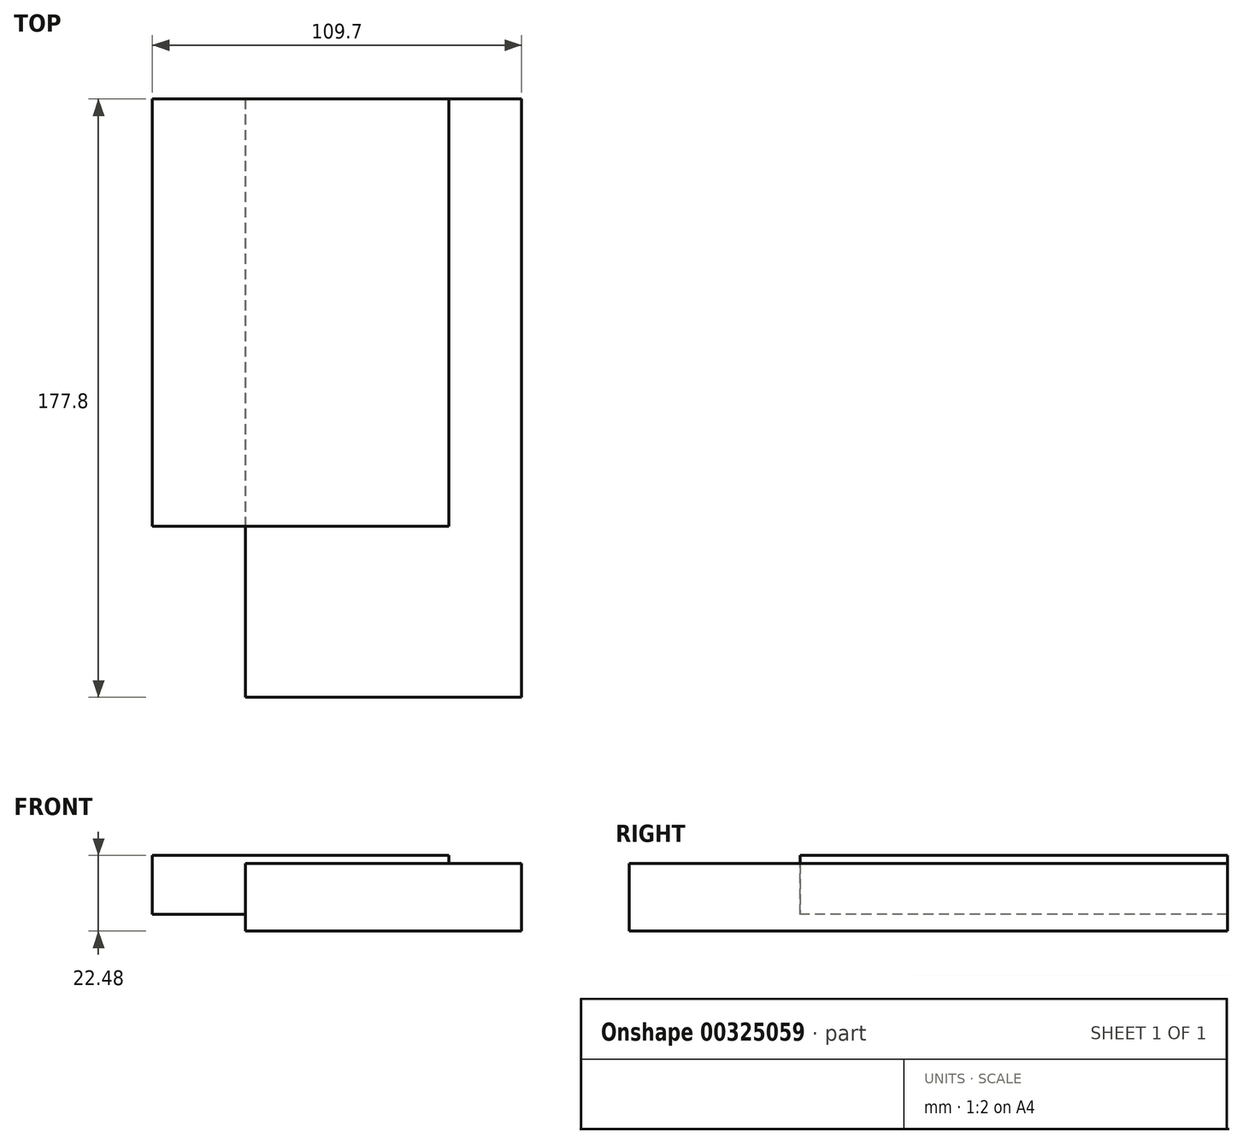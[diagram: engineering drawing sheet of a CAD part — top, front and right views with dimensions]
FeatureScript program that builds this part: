
annotation { "Feature Type Name" : "Feature", "Feature Type Description" : "" }
export const myFeature = defineFeature(function(context is Context, id is Id, definition is map)
    precondition{}
    {
        {
            var Q0;
            Q0=qCreatedBy(makeId("Front.planeOp"),FACE);
            var sketch = newSketch(context, id + "F0", { "sketchPlane" : qUnion([Q0])});
            skLineSegment(sketch, "E0.bottom", {"start": v(-44.52, 20.1) * mm, "end": v(37.55, 20.1) * mm});
            skLineSegment(sketch, "E0.top", {"start": v(-44.52, 0) * mm, "end": v(37.55, 0) * mm});
            skLineSegment(sketch, "E0.left", {"start": v(-44.52, 20.1) * mm, "end": v(-44.52, 0) * mm});
            skLineSegment(sketch, "E0.right", {"start": v(37.55, 20.1) * mm, "end": v(37.55, 0) * mm});
            skSolve(sketch);
        }
        {
            var Q0;
            Q0 = qSketchRegion(id + "F0", true);
            var sketch = newSketch(context, id + "F1", { "sketchPlane" : qUnion([Q0])});
            skSolve(sketch);
        }
        {
            var Q0;
            Q0=makeQuery(id+"F1.imprint","IMPRINT",FACE,{"disambiguationData":[TD([[makeQuery(id+"F1.imprint","IMPRINT",EDGE,{"derivedFrom":makeQuery(id+"F0.imprint","IMPRINT",EDGE,{"derivedFrom":sQuery(id+"F0.wireOp",EDGE,"E0.bottom")})}),-1.0]])]});
            extrude(context, id + "F2", {"entities" : qUnion([Q0]), "depth" : 50.8 * mm});
        }
        {
            var Q0;
            Q0=makeQuery(id+"F0.imprint","IMPRINT",FACE,{"disambiguationData":[TD([[makeQuery(id+"F0.imprint","IMPRINT",EDGE,{"derivedFrom":sQuery(id+"F0.wireOp",EDGE,"E0.bottom")}),-1.0]])]});
            var sketch = newSketch(context, id + "F3", { "sketchPlane" : qUnion([Q0])});
            skLineSegment(sketch, "E1.bottom", {"start": v(16, 5.03) * mm, "end": v(-72.15, 5.03) * mm});
            skLineSegment(sketch, "E1.top", {"start": v(16, 22.48) * mm, "end": v(-72.15, 22.48) * mm});
            skLineSegment(sketch, "E1.left", {"start": v(16, 5.03) * mm, "end": v(16, 22.48) * mm});
            skLineSegment(sketch, "E1.right", {"start": v(-72.15, 5.03) * mm, "end": v(-72.15, 22.48) * mm});
            skPoint(sketch, "E1.middle", {"position": v(-28.08, 13.76) * mm});
            skSolve(sketch);
        }
        {
            var Q0;
            {var subQ2=sQuery(id+"F3.wireOp",EDGE,"E1.top");Q0=makeQuery(id+"F3.imprint","IMPRINT",FACE,{"disambiguationData":[TD([[makeQuery(id+"F3.imprint","IMPRINT",EDGE,{"derivedFrom":subQ2}),1.0]])]});}
            var Q1;
            Q1=makeQuery(id+"F0.imprint","IMPRINT",FACE,{"disambiguationData":[TD([[makeQuery(id+"F0.imprint","IMPRINT",EDGE,{"derivedFrom":sQuery(id+"F0.wireOp",EDGE,"E0.bottom")}),-1.0]])]});
            extrude(context, id + "F4", {"entities" : qUnion([Q0, Q1]), "operationType" : NewBodyOperationType.ADD, "depth" : -127 * mm});
        }
    });
